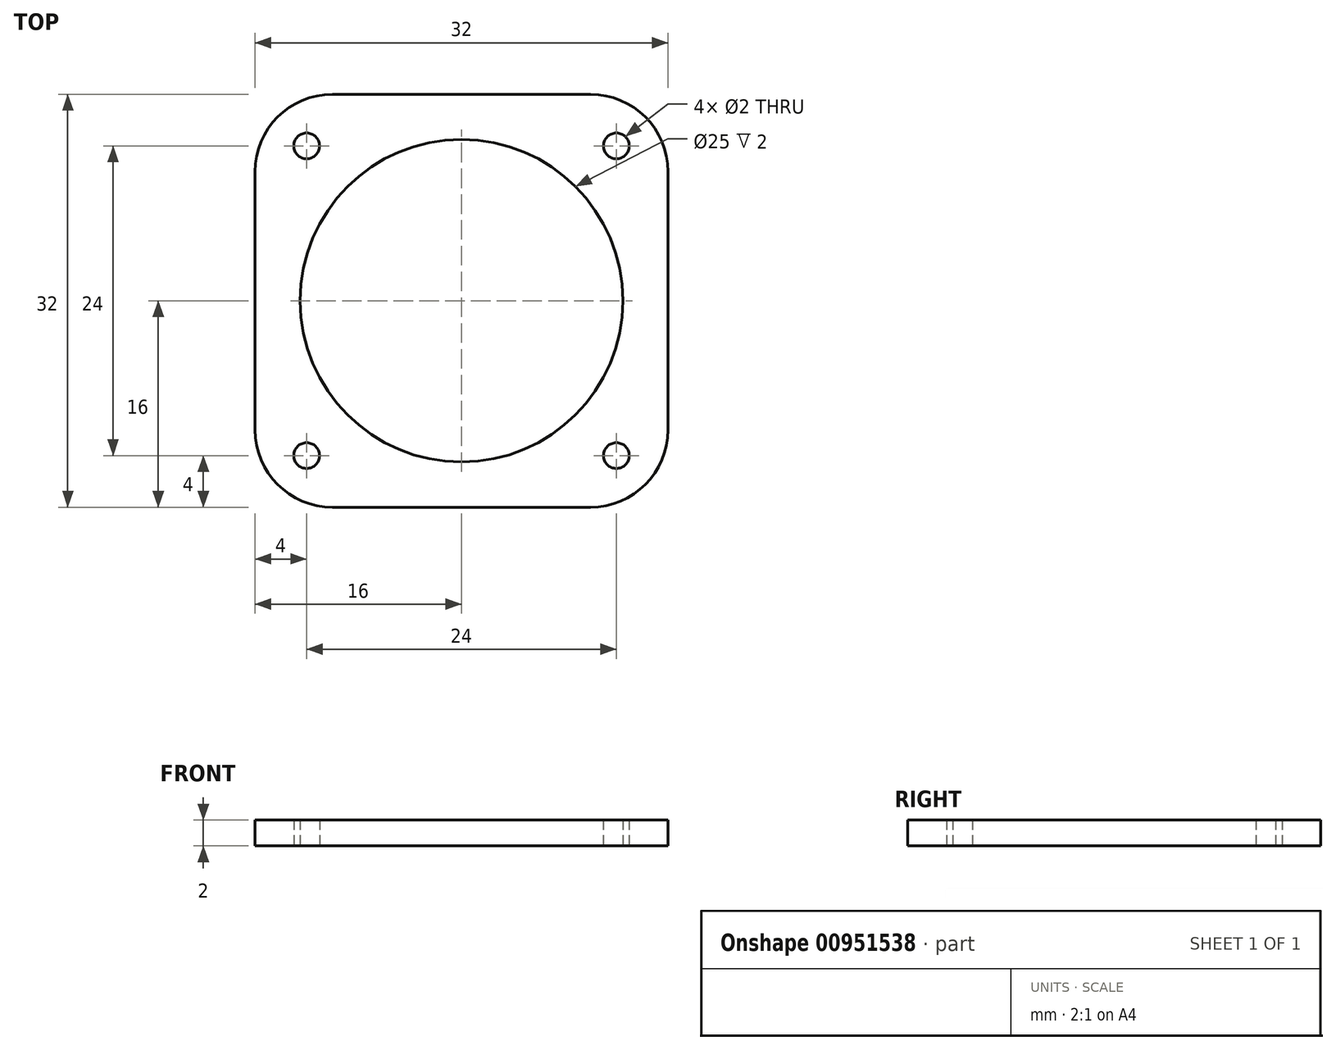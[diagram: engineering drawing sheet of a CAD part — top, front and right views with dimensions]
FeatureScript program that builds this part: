
annotation { "Feature Type Name" : "Feature", "Feature Type Description" : "" }
export const myFeature = defineFeature(function(context is Context, id is Id, definition is map)
    precondition{}
    {
        {
            var Q0;
            Q0=qCreatedBy(makeId("Top.planeOp"),FACE);
            var sketch = newSketch(context, id + "F0", { "sketchPlane" : qUnion([Q0])});
            skLineSegment(sketch, "E0.bottom", {"start": v(-10, 16) * mm, "end": v(10, 16) * mm});
            skLineSegment(sketch, "E0.top", {"start": v(-10, -16) * mm, "end": v(10, -16) * mm});
            skLineSegment(sketch, "E0.left", {"start": v(-16, 10) * mm, "end": v(-16, -10) * mm});
            skLineSegment(sketch, "E0.right", {"start": v(16, 10) * mm, "end": v(16, -10) * mm});
            skPoint(sketch, "E0.middle", {"position": v(0, 0) * mm});
            skCircle(sketch, "E1", {"center": v(0, 0) * mm, "radius": 12.5 * mm});
            skCircle(sketch, "E2", {"center": v(12, 12) * mm, "radius": 1 * mm});
            skCircle(sketch, "E3", {"center": v(-12, 12) * mm, "radius": 1 * mm});
            skCircle(sketch, "E4", {"center": v(-12, -12) * mm, "radius": 1 * mm});
            skCircle(sketch, "E5", {"center": v(12, -12) * mm, "radius": 1 * mm});
            skPoint(sketch, "E6.visualSharp", {"position": v(16, 16) * mm});
            skArc(sketch, "E6.filletArc", {"start": v(16, 10) * mm, "mid": v(14.24, 14.24) * mm, "end": v(10, 16) * mm});
            skPoint(sketch, "E7.visualSharp", {"position": v(16, -16) * mm});
            skArc(sketch, "E7.filletArc", {"start": v(10, -16) * mm, "mid": v(14.24, -14.24) * mm, "end": v(16, -10) * mm});
            skPoint(sketch, "E8.visualSharp", {"position": v(-16, -16) * mm});
            skArc(sketch, "E8.filletArc", {"start": v(-16, -10) * mm, "mid": v(-14.24, -14.24) * mm, "end": v(-10, -16) * mm});
            skPoint(sketch, "E9.visualSharp", {"position": v(-16, 16) * mm});
            skArc(sketch, "E9.filletArc", {"start": v(-10, 16) * mm, "mid": v(-14.24, 14.24) * mm, "end": v(-16, 10) * mm});
            skSolve(sketch);
        }
        {
            var Q0;
            Q0 = qSketchRegion(id + "F0", true);
            extrude(context, id + "F1", {"entities" : qUnion([Q0]), "depth" : 2 * mm, "offsetDistance" : 25 * mm});
        }
    });
